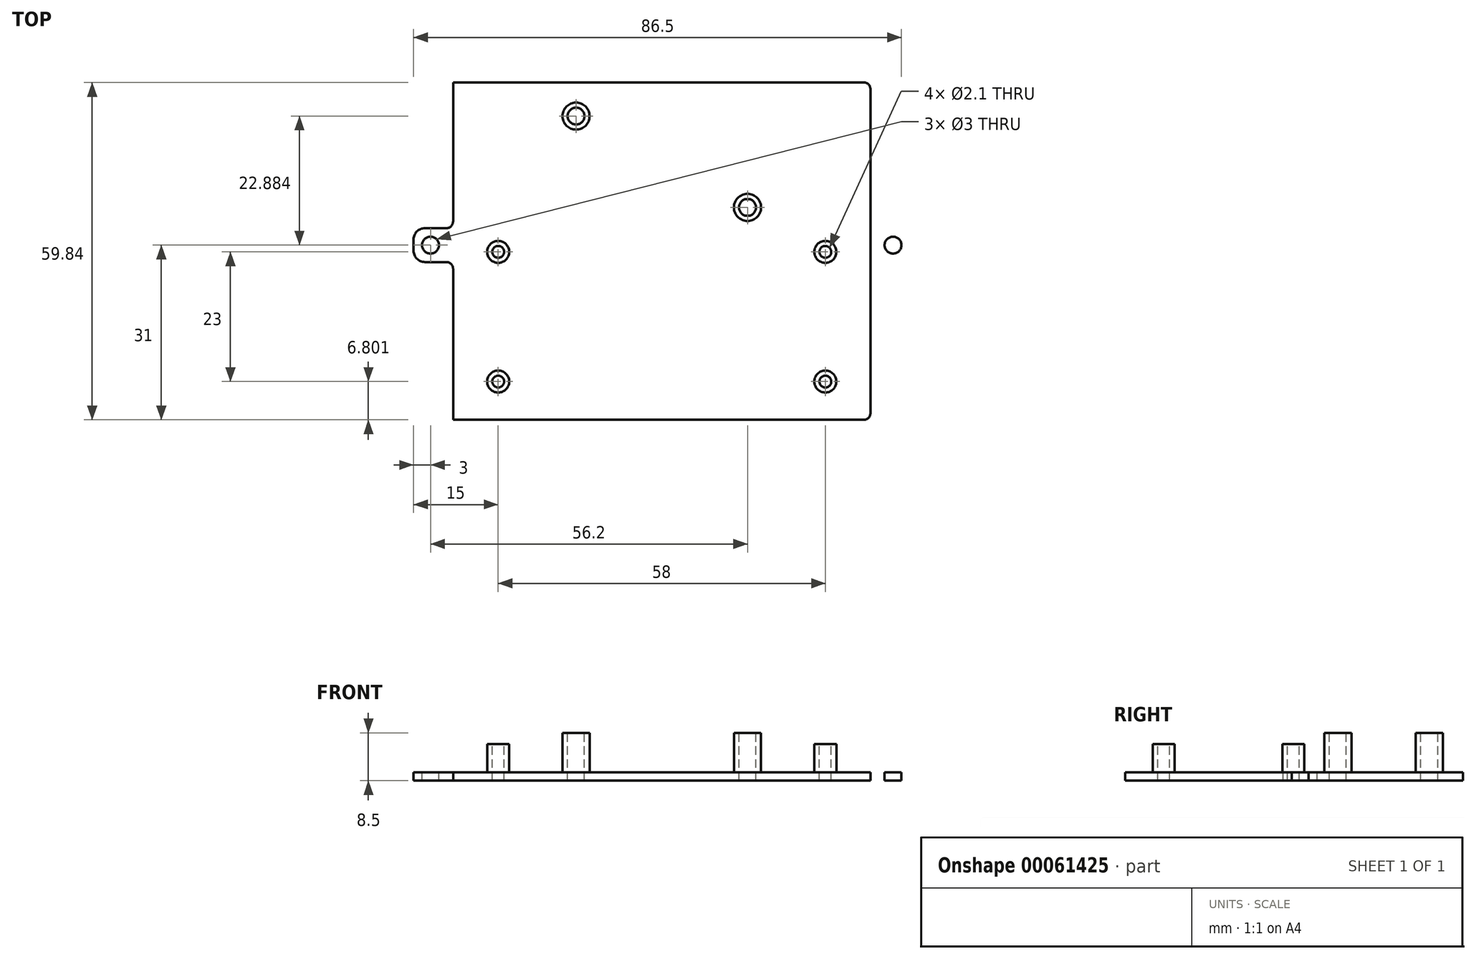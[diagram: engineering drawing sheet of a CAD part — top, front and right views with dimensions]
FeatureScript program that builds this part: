
annotation { "Feature Type Name" : "Feature", "Feature Type Description" : "" }
export const myFeature = defineFeature(function(context is Context, id is Id, definition is map)
    precondition{}
    {
        {
            var Q0;
            Q0=qCreatedBy(makeId("Top.planeOp"),FACE);
            var sketch = newSketch(context, id + "F0", { "sketchPlane" : qUnion([Q0])});
            skPoint(sketch, "E0.rect.middle", {"position": v(0, 0) * mm});
            skLineSegment(sketch, "E1.rect.bottom", {"start": v(-29, 0.48) * mm, "end": v(29, 0.48) * mm, "construction": true});
            skLineSegment(sketch, "E1.rect.top", {"start": v(-29, -22.52) * mm, "end": v(29, -22.52) * mm, "construction": true});
            skLineSegment(sketch, "E1.rect.left", {"start": v(-29, 0.48) * mm, "end": v(-29, -22.52) * mm, "construction": true});
            skLineSegment(sketch, "E1.rect.right", {"start": v(29, 0.48) * mm, "end": v(29, -22.52) * mm, "construction": true});
            skPoint(sketch, "E1.rect.middle", {"position": v(0, -11.02) * mm});
            skCircle(sketch, "E2", {"center": v(-29, -22.52) * mm, "radius": 1.05 * mm});
            skCircle(sketch, "E3", {"center": v(-29, 0.48) * mm, "radius": 1.05 * mm});
            skCircle(sketch, "E4", {"center": v(29, 0.48) * mm, "radius": 1.05 * mm});
            skCircle(sketch, "E5", {"center": v(29, -22.52) * mm, "radius": 1.05 * mm});
            skLineSegment(sketch, "E6.rect.bottom", {"start": v(21.5, 5.96) * mm, "end": v(-21.5, 5.96) * mm, "construction": true});
            skLineSegment(sketch, "E6.rect.top", {"start": v(21.5, 26.96) * mm, "end": v(-21.5, 26.96) * mm, "construction": true});
            skLineSegment(sketch, "E6.rect.left", {"start": v(21.5, 5.96) * mm, "end": v(21.5, 26.96) * mm, "construction": true});
            skLineSegment(sketch, "E6.rect.right", {"start": v(-21.5, 5.96) * mm, "end": v(-21.5, 26.96) * mm, "construction": true});
            skPoint(sketch, "E6.rect.middle", {"position": v(0, 16.46) * mm});
            skCircle(sketch, "E7", {"center": v(-15.2, 24.56) * mm, "radius": 1.5 * mm});
            skCircle(sketch, "E8", {"center": v(15.2, 8.36) * mm, "radius": 1.5 * mm});
            skLineSegment(sketch, "E9.bottom", {"start": v(-37, 30.52) * mm, "end": v(37, 30.52) * mm});
            skLineSegment(sketch, "E9.top", {"start": v(-37, -29.32) * mm, "end": v(37, -29.32) * mm});
            skLineSegment(sketch, "E9.left", {"start": v(-37, 30.52) * mm, "end": v(-37, -29.32) * mm});
            skLineSegment(sketch, "E9.right", {"start": v(37, 30.52) * mm, "end": v(37, -29.32) * mm});
            skLineSegment(sketch, "E10", {"start": v(0, 30.52) * mm, "end": v(0, -29.32) * mm, "construction": true});
            skLineSegment(sketch, "E11.rect.bottom", {"start": v(-42, 4.68) * mm, "end": v(-37, 4.68) * mm});
            skLineSegment(sketch, "E11.rect.top", {"start": v(-42, -1.32) * mm, "end": v(-37, -1.32) * mm});
            skLineSegment(sketch, "E11.rect.left", {"start": v(-44, 2.68) * mm, "end": v(-44, 0.68) * mm});
            skLineSegment(sketch, "E11.rect.right", {"start": v(-37, 4.68) * mm, "end": v(-37, -1.32) * mm});
            skPoint(sketch, "E11.rect.middle", {"position": v(-40.5, 1.68) * mm});
            skCircle(sketch, "E12", {"center": v(-41, 1.68) * mm, "radius": 1.5 * mm});
            skPoint(sketch, "E13.visualSharp", {"position": v(-44, 4.68) * mm});
            skArc(sketch, "E13.filletArc", {"start": v(-42, 4.68) * mm, "mid": v(-43.41, 4.1) * mm, "end": v(-44, 2.68) * mm});
            skPoint(sketch, "E14.visualSharp", {"position": v(-44, -1.32) * mm});
            skArc(sketch, "E14.filletArc", {"start": v(-44, 0.68) * mm, "mid": v(-43.41, -0.73) * mm, "end": v(-42, -1.32) * mm});
            skPoint(sketch, "E15.MirrorP", {"position": v(44, -1.32) * mm});
            skPoint(sketch, "E16.MirrorP", {"position": v(41, 1.68) * mm});
            skCircle(sketch, "E17.MirrorC", {"center": v(41, 1.68) * mm, "radius": 1.5 * mm});
            skLineSegment(sketch, "E18.MirrorCS", {"start": v(44, 2.68) * mm, "end": v(44, 0.68) * mm});
            skPoint(sketch, "E19.MirrorP", {"position": v(44, 4.68) * mm});
            skArc(sketch, "E20.MirrorCS", {"start": v(42, 4.68) * mm, "mid": v(43.41, 4.1) * mm, "end": v(44, 2.68) * mm});
            skArc(sketch, "E21.MirrorCS", {"start": v(44, 0.68) * mm, "mid": v(43.41, -0.73) * mm, "end": v(42, -1.32) * mm});
            skLineSegment(sketch, "E22.MirrorCS", {"start": v(42, -1.32) * mm, "end": v(37, -1.32) * mm});
            skLineSegment(sketch, "E23.MirrorCS", {"start": v(42, 4.68) * mm, "end": v(37, 4.68) * mm});
            skSolve(sketch);
        }
        {
            var Q0;
            Q0=makeQuery(id+"F0.imprint","IMPRINT",FACE,{"disambiguationData":[TD([[makeQuery(id+"F0.imprint","IMPRINT",EDGE,{"derivedFrom":sQuery(id+"F0.wireOp",EDGE,"E2")}),-1.0]])]});
            var Q1;
            Q1=makeQuery(id+"F0.imprint","IMPRINT",FACE,{"disambiguationData":[TD([[makeQuery(id+"F0.imprint","IMPRINT",EDGE,{"derivedFrom":sQuery(id+"F0.wireOp",EDGE,"E11.rect.bottom")}),-1.0]])]});
            var Q2;
            Q2=makeQuery(id+"F0.imprint","IMPRINT",FACE,{"disambiguationData":[TD([[makeQuery(id+"F0.imprint","IMPRINT",EDGE,{"derivedFrom":sQuery(id+"F0.wireOp",EDGE,"E17.MirrorC")}),1.0]])]});
            extrude(context, id + "F1", {"entities" : qUnion([Q0, Q1, Q2]), "oppositeDirection" : true, "depth" : 1.5 * mm});
        }
        {
            var Q0;
            Q0=makeQuery(id+"F1.opExtrude","CAP_FACE",FACE,{"disambiguationData":[OSD([sQuery(id+"F0.wireOp",EDGE,"E2"),sQuery(id+"F0.wireOp",EDGE,"E3"),sQuery(id+"F0.wireOp",EDGE,"E4"),sQuery(id+"F0.wireOp",EDGE,"E5"),sQuery(id+"F0.wireOp",EDGE,"E7"),sQuery(id+"F0.wireOp",EDGE,"E8"),sQuery(id+"F0.wireOp",EDGE,"E9.bottom"),sQuery(id+"F0.wireOp",EDGE,"E9.top"),sQuery(id+"F0.wireOp",EDGE,"E9.left"),sQuery(id+"F0.wireOp",EDGE,"E9.right")])],"isStart":true});
            var sketch = newSketch(context, id + "F2", { "sketchPlane" : qUnion([Q0])});
            skLineSegment(sketch, "E24.0", {"start": v(-36.2, 29.72) * mm, "end": v(36.2, 29.72) * mm});
            skLineSegment(sketch, "E24.1", {"start": v(-36.2, 29.72) * mm, "end": v(-36.2, -28.52) * mm});
            skLineSegment(sketch, "E24.2", {"start": v(-36.2, -28.52) * mm, "end": v(36.2, -28.52) * mm});
            skLineSegment(sketch, "E24.3", {"start": v(36.2, 29.72) * mm, "end": v(36.2, -28.52) * mm});
            skLineSegment(sketch, "E25", {"start": v(-37, 4.68) * mm, "end": v(-37, -1.32) * mm});
            skLineSegment(sketch, "E26", {"start": v(37, 4.68) * mm, "end": v(37, -1.32) * mm});
            skPoint(sketch, "E27.0", {"position": v(0, 0) * mm});
            skLineSegment(sketch, "E27.1", {"start": v(-29, 0.48) * mm, "end": v(29, 0.48) * mm});
            skLineSegment(sketch, "E27.2", {"start": v(-29, -22.52) * mm, "end": v(29, -22.52) * mm});
            skLineSegment(sketch, "E27.3", {"start": v(-29, 0.48) * mm, "end": v(-29, -22.52) * mm});
            skLineSegment(sketch, "E27.4", {"start": v(29, 0.48) * mm, "end": v(29, -22.52) * mm});
            skPoint(sketch, "E27.5", {"position": v(0, -11.02) * mm});
            skCircle(sketch, "E27.6", {"center": v(-29, -22.52) * mm, "radius": 1.05 * mm});
            skCircle(sketch, "E27.7", {"center": v(-29, 0.48) * mm, "radius": 1.05 * mm});
            skCircle(sketch, "E27.8", {"center": v(29, 0.48) * mm, "radius": 1.05 * mm});
            skCircle(sketch, "E27.9", {"center": v(29, -22.52) * mm, "radius": 1.05 * mm});
            skLineSegment(sketch, "E27.10", {"start": v(21.5, 5.96) * mm, "end": v(-21.5, 5.96) * mm});
            skLineSegment(sketch, "E27.11", {"start": v(21.5, 26.96) * mm, "end": v(-21.5, 26.96) * mm});
            skLineSegment(sketch, "E27.12", {"start": v(21.5, 5.96) * mm, "end": v(21.5, 26.96) * mm});
            skLineSegment(sketch, "E27.13", {"start": v(-21.5, 5.96) * mm, "end": v(-21.5, 26.96) * mm});
            skPoint(sketch, "E27.14", {"position": v(0, 16.46) * mm});
            skCircle(sketch, "E27.15", {"center": v(-15.2, 24.56) * mm, "radius": 1.5 * mm});
            skCircle(sketch, "E27.16", {"center": v(15.2, 8.36) * mm, "radius": 1.5 * mm});
            skLineSegment(sketch, "E27.17", {"start": v(-37, 30.52) * mm, "end": v(37, 30.52) * mm});
            skLineSegment(sketch, "E27.18", {"start": v(-37, -29.32) * mm, "end": v(37, -29.32) * mm});
            skLineSegment(sketch, "E27.19", {"start": v(-37, 30.52) * mm, "end": v(-37, -29.32) * mm});
            skLineSegment(sketch, "E27.20", {"start": v(37, 30.52) * mm, "end": v(37, -29.32) * mm});
            skLineSegment(sketch, "E27.21", {"start": v(0, 30.52) * mm, "end": v(0, -29.32) * mm, "construction": true});
            skLineSegment(sketch, "E27.22", {"start": v(-42, 4.68) * mm, "end": v(-37, 4.68) * mm});
            skLineSegment(sketch, "E27.23", {"start": v(-42, -1.32) * mm, "end": v(-37, -1.32) * mm});
            skLineSegment(sketch, "E27.24", {"start": v(-44, 2.68) * mm, "end": v(-44, 0.68) * mm});
            skPoint(sketch, "E27.26", {"position": v(-40.5, 1.68) * mm});
            skCircle(sketch, "E27.27", {"center": v(-41, 1.68) * mm, "radius": 1.5 * mm});
            skPoint(sketch, "E27.28", {"position": v(-44, 4.68) * mm});
            skArc(sketch, "E27.29", {"start": v(-42, 4.68) * mm, "mid": v(-43.41, 4.1) * mm, "end": v(-44, 2.68) * mm});
            skPoint(sketch, "E27.30", {"position": v(-44, -1.32) * mm});
            skArc(sketch, "E27.31", {"start": v(-44, 0.68) * mm, "mid": v(-43.41, -0.73) * mm, "end": v(-42, -1.32) * mm});
            skPoint(sketch, "E27.32", {"position": v(44, -1.32) * mm});
            skPoint(sketch, "E27.33", {"position": v(41, 1.68) * mm});
            skCircle(sketch, "E27.34", {"center": v(41, 1.68) * mm, "radius": 1.5 * mm});
            skLineSegment(sketch, "E27.35", {"start": v(44, 2.68) * mm, "end": v(44, 0.68) * mm});
            skPoint(sketch, "E27.36", {"position": v(44, 4.68) * mm});
            skArc(sketch, "E27.37", {"start": v(42, 4.68) * mm, "mid": v(43.41, 4.1) * mm, "end": v(44, 2.68) * mm});
            skArc(sketch, "E27.38", {"start": v(44, 0.68) * mm, "mid": v(43.41, -0.73) * mm, "end": v(42, -1.32) * mm});
            skLineSegment(sketch, "E27.39", {"start": v(42, -1.32) * mm, "end": v(37, -1.32) * mm});
            skLineSegment(sketch, "E27.40", {"start": v(42, 4.68) * mm, "end": v(37, 4.68) * mm});
            skLineSegment(sketch, "E28", {"start": v(10, -24.72) * mm, "end": v(10, -29.61) * mm, "construction": true});
            skLineSegment(sketch, "E29.rect.bottom", {"start": v(0.5, -25.12) * mm, "end": v(19.5, -25.12) * mm});
            skLineSegment(sketch, "E29.rect.top", {"start": v(0.5, -34.1) * mm, "end": v(19.5, -34.1) * mm});
            skLineSegment(sketch, "E29.rect.left", {"start": v(0.5, -25.12) * mm, "end": v(0.5, -34.1) * mm});
            skLineSegment(sketch, "E29.rect.right", {"start": v(19.5, -25.12) * mm, "end": v(19.5, -34.1) * mm});
            skPoint(sketch, "E29.rect.middle", {"position": v(10, -29.61) * mm});
            skLineSegment(sketch, "E30.rect.bottom", {"start": v(-39.84, 24.52) * mm, "end": v(-34.16, 24.52) * mm});
            skLineSegment(sketch, "E30.rect.top", {"start": v(-39.84, 8.52) * mm, "end": v(-34.16, 8.52) * mm});
            skLineSegment(sketch, "E30.rect.left", {"start": v(-39.84, 24.52) * mm, "end": v(-39.84, 8.52) * mm});
            skLineSegment(sketch, "E30.rect.right", {"start": v(-34.16, 24.52) * mm, "end": v(-34.16, 8.52) * mm});
            skPoint(sketch, "E30.rect.middle", {"position": v(-37, 16.52) * mm});
            skSolve(sketch);
        }
        {
            var Q0;
            Q0=makeQuery(id+"F4of1dtIsf2Vx9E_1.opExtrude","CAP_EDGE",EDGE,{"disambiguationData":[OSD([sQuery(id+"F0.wireOp",EDGE,"E9.left"),sQuery(id+"F2.wireOp",EDGE,"E25")])],"isStart":true});
            var Q1;
            Q1=makeQuery(id+"F1.opExtrude","SWEPT_EDGE",EDGE,{"disambiguationData":[OSD([sQuery(id+"F0.wireOp",EDGE,"E9.left"),sQuery(id+"F0.wireOp",EDGE,"E11.rect.top"),sQuery(id+"F0.wireOp",EDGE,"E11.rect.right")])]});
            var Q2;
            Q2=makeQuery(id+"F1.opExtrude","SWEPT_EDGE",EDGE,{"disambiguationData":[OSD([sQuery(id+"F0.wireOp",EDGE,"E9.left"),sQuery(id+"F0.wireOp",EDGE,"E11.rect.bottom"),sQuery(id+"F0.wireOp",EDGE,"E11.rect.right")])]});
            var Q3;
            Q3=makeQuery(id+"F4of1dtIsf2Vx9E_1.opExtrude","CAP_EDGE",EDGE,{"disambiguationData":[OSD([sQuery(id+"F0.wireOp",EDGE,"E9.right"),sQuery(id+"F2.wireOp",EDGE,"E26")])],"isStart":true});
            var Q4;
            Q4=makeQuery(id+"F1.opExtrude","SWEPT_EDGE",EDGE,{"disambiguationData":[OSD([sQuery(id+"F0.wireOp",EDGE,"E9.right"),sQuery(id+"F0.wireOp",EDGE,"E22.MirrorCS")])]});
            var Q5;
            Q5=makeQuery(id+"F1.opExtrude","SWEPT_EDGE",EDGE,{"disambiguationData":[OSD([sQuery(id+"F0.wireOp",EDGE,"E9.right"),sQuery(id+"F0.wireOp",EDGE,"E23.MirrorCS")])]});
            fillet(context, id + "F3", {"entities" : qUnion([Q0, Q1, Q2, Q3, Q4, Q5]), "radius" : 1.2 * mm, "tangentPropagation" : true, "allowEdgeOverflow" : false});
        }
        {
            var Q0;
            {var subQ3=sQuery(id+"F0.wireOp",EDGE,"E4");var subQ4=sQuery(id+"F0.wireOp",EDGE,"E9.top");var subQ5=sQuery(id+"F0.wireOp",EDGE,"E8");var subQ8=sQuery(id+"F0.wireOp",EDGE,"E7");var subQ9=sQuery(id+"F0.wireOp",EDGE,"E2");var subQ10=sQuery(id+"F0.wireOp",EDGE,"E3");var subQ11=sQuery(id+"F0.wireOp",EDGE,"E5");Q0=makeQuery(id+"F4of1dtIsf2Vx9E_1.boolean.opBoolean","SPLIT",FACE,{"disambiguationData":[TD([makeQuery(id+"F1.opExtrude","SWEPT_FACE",FACE,{"disambiguationData":[OSD([subQ9])]})])],"derivedFrom":makeQuery(id+"F1.opExtrude","CAP_FACE",FACE,{"disambiguationData":[OSD([subQ9,subQ10,subQ3,subQ11,subQ8,subQ5,sQuery(id+"F0.wireOp",EDGE,"E9.bottom"),subQ4,sQuery(id+"F0.wireOp",EDGE,"E9.left"),sQuery(id+"F0.wireOp",EDGE,"E9.right"),sQuery(id+"F0.wireOp",EDGE,"E11.rect.bottom"),sQuery(id+"F0.wireOp",EDGE,"E11.rect.top"),sQuery(id+"F0.wireOp",EDGE,"E11.rect.left"),sQuery(id+"F0.wireOp",EDGE,"E12"),sQuery(id+"F0.wireOp",EDGE,"E13.filletArc"),sQuery(id+"F0.wireOp",EDGE,"E14.filletArc"),sQuery(id+"F0.wireOp",EDGE,"E17.MirrorC"),sQuery(id+"F0.wireOp",EDGE,"E18.MirrorCS"),sQuery(id+"F0.wireOp",EDGE,"E20.MirrorCS"),sQuery(id+"F0.wireOp",EDGE,"E21.MirrorCS"),sQuery(id+"F0.wireOp",EDGE,"E22.MirrorCS"),sQuery(id+"F0.wireOp",EDGE,"E23.MirrorCS")])],"isStart":true})});}
            var sketch = newSketch(context, id + "F4", { "sketchPlane" : qUnion([Q0])});
            skCircle(sketch, "E31", {"center": v(-15.2, 24.56) * mm, "radius": 2.4 * mm});
            skCircle(sketch, "E32", {"center": v(-29, 0.48) * mm, "radius": 1.95 * mm});
            skCircle(sketch, "E33", {"center": v(-29, -22.52) * mm, "radius": 1.95 * mm});
            skCircle(sketch, "E34", {"center": v(29, -22.52) * mm, "radius": 1.95 * mm});
            skCircle(sketch, "E35", {"center": v(29, 0.48) * mm, "radius": 1.95 * mm});
            skCircle(sketch, "E36", {"center": v(15.2, 8.36) * mm, "radius": 2.4 * mm});
            skSolve(sketch);
        }
        {
            var Q0;
            Q0=makeQuery(id+"F4.imprint","IMPRINT",FACE,{"disambiguationData":[TD([[makeQuery(id+"F4.imprint","IMPRINT",EDGE,{"derivedFrom":sQuery(id+"F4.wireOp",EDGE,"E32")}),1.0]])]});
            var Q1;
            Q1=makeQuery(id+"F4.imprint","IMPRINT",FACE,{"disambiguationData":[TD([[makeQuery(id+"F4.imprint","IMPRINT",EDGE,{"derivedFrom":sQuery(id+"F4.wireOp",EDGE,"E33")}),1.0]])]});
            var Q2;
            Q2=makeQuery(id+"F4.imprint","IMPRINT",FACE,{"disambiguationData":[TD([[makeQuery(id+"F4.imprint","IMPRINT",EDGE,{"derivedFrom":sQuery(id+"F4.wireOp",EDGE,"E34")}),1.0]])]});
            var Q3;
            Q3=makeQuery(id+"F4.imprint","IMPRINT",FACE,{"disambiguationData":[TD([[makeQuery(id+"F4.imprint","IMPRINT",EDGE,{"derivedFrom":sQuery(id+"F4.wireOp",EDGE,"E35")}),1.0]])]});
            extrude(context, id + "F5", {"entities" : qUnion([Q0, Q1, Q2, Q3]), "operationType" : NewBodyOperationType.ADD, "depth" : 5 * mm});
        }
        {
            var Q0;
            Q0=makeQuery(id+"F4.imprint","IMPRINT",FACE,{"disambiguationData":[TD([[makeQuery(id+"F4.imprint","IMPRINT",EDGE,{"derivedFrom":sQuery(id+"F4.wireOp",EDGE,"E31")}),1.0]])]});
            var Q1;
            Q1=makeQuery(id+"F4.imprint","IMPRINT",FACE,{"disambiguationData":[TD([[makeQuery(id+"F4.imprint","IMPRINT",EDGE,{"derivedFrom":sQuery(id+"F4.wireOp",EDGE,"E36")}),1.0]])]});
            extrude(context, id + "F6", {"entities" : qUnion([Q0, Q1]), "operationType" : NewBodyOperationType.ADD, "depth" : 7 * mm});
        }
    });
